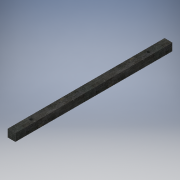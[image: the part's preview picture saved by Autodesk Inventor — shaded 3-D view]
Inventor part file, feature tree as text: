
AUTODESK INVENTOR PART (.ipt)
format: ipt  version: 2019 (Build 230136000, 136)  size: 113,664 bytes
history: native  units: mm
features: extrude x2, sketch x2
ambient origin geometry x8: Origin, YZ Plane, XZ Plane, XY Plane, X Axis, Y Axis, Z Axis, Center Point
bodies: Solid1 (feature_tree)
feature tree (4):
  extrude  "Extrusion1"  Depth=395.0mm
  extrude  "Extrusion2"  Depth=19.0mm
  sketch  "Sketch1"  dims[d0=19.0mm d1=395.0mm]
  sketch  "Sketch2"  dims[d2=19.0mm d3=0.0mm d4=8.0mm d5=8.0mm d6=50.0mm d7=9.5mm d8=9.5mm d9=50.0mm d10=19.0mm d11=0.0mm]
